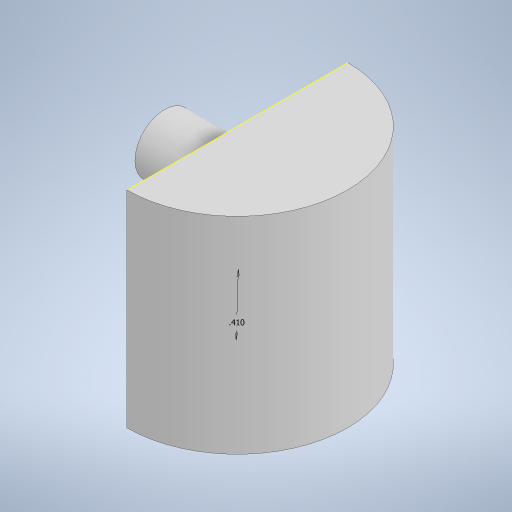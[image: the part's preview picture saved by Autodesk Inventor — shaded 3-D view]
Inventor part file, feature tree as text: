
AUTODESK INVENTOR PART (.ipt)
format: ipt  version: 2023 (Build 270158000, 158)  size: 210,432 bytes
history: native  units: in
note: dims shown in document units (in); Inventor stores cm internally (conversion verified against a paired STEP export)
features: extrude x3, sketch x2
ambient origin geometry x8: Origin, YZ Plane, XZ Plane, XY Plane, X Axis, Y Axis, Z Axis, Center Point
bodies: Solid1 (feature_tree)
feature tree (5):
  extrude  "Extrusion1"  Depth=1.4in TaperAngle=0.0deg
  sketch  "Sketch2"  dims[d4=0.5in d5=0.0in d6=0.41in d7=0.495in d8=0.0in]
  extrude  "Extrusion2"  Depth=0.495in
  extrude  "Extrusion3"  Depth=0.495in TaperAngle=0.0deg
  sketch  "Sketch1"  dims[d0=1.5in d1=1.4in d2=0.0in]
